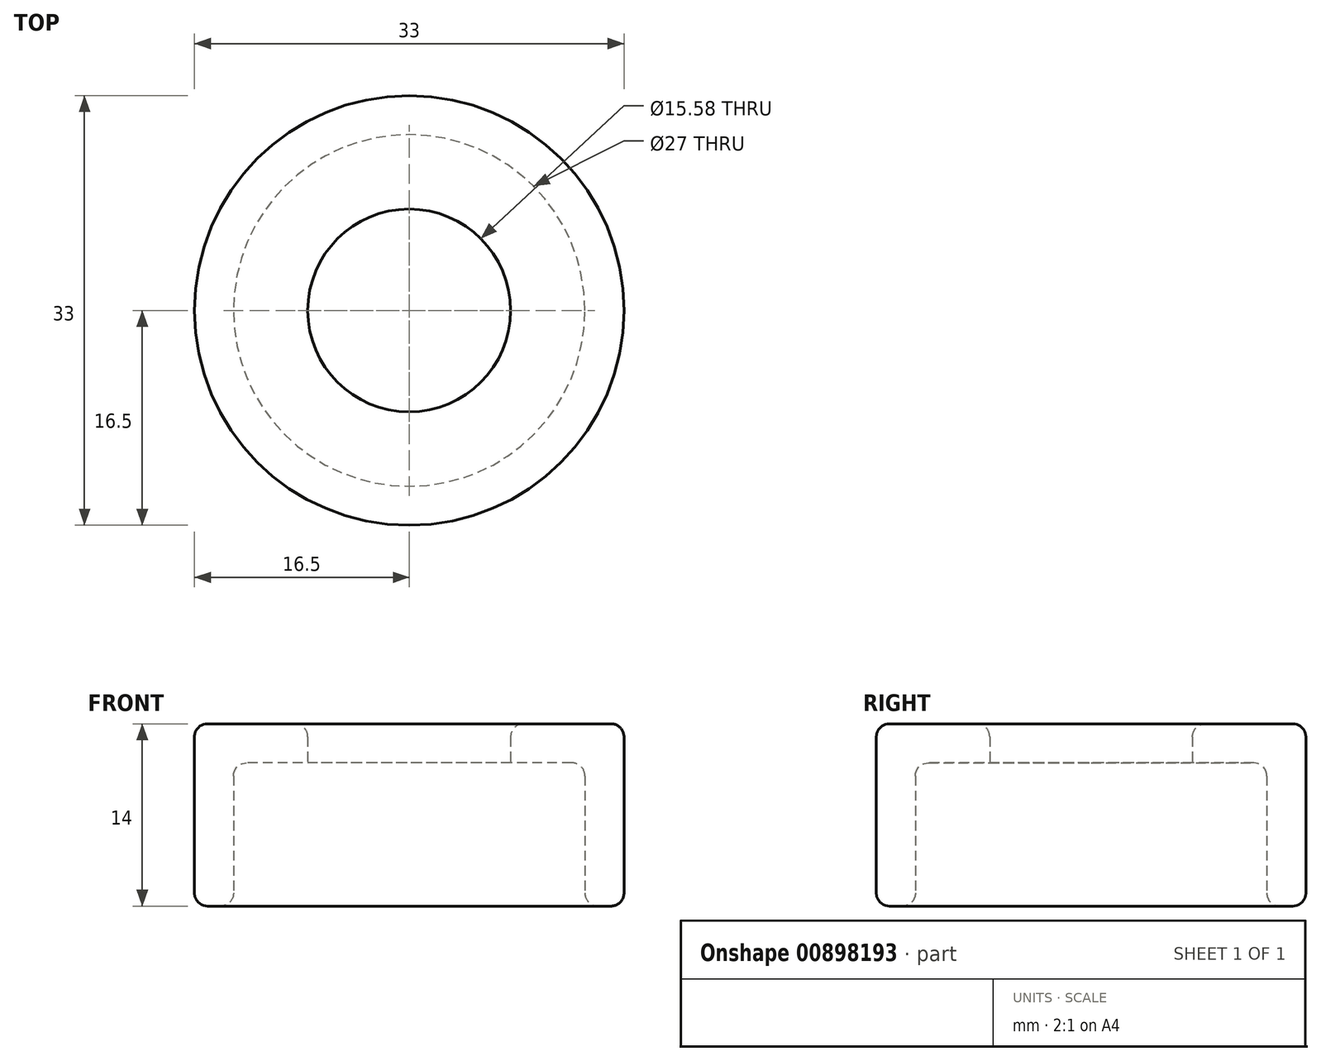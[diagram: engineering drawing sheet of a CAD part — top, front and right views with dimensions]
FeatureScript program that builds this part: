
annotation { "Feature Type Name" : "Feature", "Feature Type Description" : "" }
export const myFeature = defineFeature(function(context is Context, id is Id, definition is map)
    precondition{}
    {
        {
            var Q0;
            Q0=qCreatedBy(makeId("Front.planeOp"),FACE);
            var sketch = newSketch(context, id + "F0", { "sketchPlane" : qUnion([Q0])});
            skArc(sketch, "E0", {"start": v(4.55, -9.46) * mm, "mid": v(10.24, 2.33) * mm, "end": v(0, 10.5) * mm});
            skLineSegment(sketch, "E1.top", {"start": v(0, -17) * mm, "end": v(7, -17) * mm});
            skLineSegment(sketch, "E1.right", {"start": v(4.55, -9.46) * mm, "end": v(7, -17) * mm});
            skArc(sketch, "E2", {"start": v(10.06, -3) * mm, "mid": v(8.42, 6.27) * mm, "end": v(0, 10.5) * mm});
            skLineSegment(sketch, "E3", {"start": v(15.41, -3) * mm, "end": v(-18.62, -3) * mm, "construction": true});
            skArc(sketch, "E4", {"start": v(0, 13.5) * mm, "mid": v(10.55, 8.42) * mm, "end": v(13.16, -3) * mm});
            skLineSegment(sketch, "E5", {"start": v(-13.16, -3) * mm, "end": v(-10.06, -3) * mm});
            skLineSegment(sketch, "E6", {"start": v(10.06, -3) * mm, "end": v(13.16, -3) * mm});
            skLineSegment(sketch, "E7", {"start": v(0, -27.03) * mm, "end": v(0, 18.55) * mm, "construction": true});
            skPoint(sketch, "E8.MirrorCS.start.orphan", {"position": v(0, -17) * mm});
            skLineSegment(sketch, "E9", {"start": v(0, 13.5) * mm, "end": v(0, 10.5) * mm});
            skLineSegment(sketch, "E10", {"start": v(0, 10.5) * mm, "end": v(0, -17) * mm});
            skLineSegment(sketch, "E11", {"start": v(0, 13.5) * mm, "end": v(8, 13.5) * mm});
            skLineSegment(sketch, "E12", {"start": v(8, 13.5) * mm, "end": v(7.3, 11.36) * mm});
            skSolve(sketch);
        }
        {
            var Q0;
            {var subQ0=sQuery(id+"F0.wireOp",EDGE,"E6");var subQ4=sQuery(id+"F0.wireOp",EDGE,"E11");Q0=qUnion([makeQuery(id+"F0.imprint","IMPRINT",FACE,{"disambiguationData":[TD([[makeQuery(id+"F0.imprint","IMPRINT",EDGE,{"derivedFrom":sQuery(id+"F0.wireOp",EDGE,"E1.top")}),1.0]])]}),makeQuery(id+"F0.imprint","IMPRINT",FACE,{"disambiguationData":[TD([[makeQuery(id+"F0.imprint","IMPRINT",EDGE,{"derivedFrom":subQ4}),-1.0]])]}),makeQuery(id+"F0.imprint","IMPRINT",FACE,{"disambiguationData":[TD([[makeQuery(id+"F0.imprint","IMPRINT",EDGE,{"derivedFrom":subQ0}),1.0]])]})]);}
            var Q1;
            Q1=sQuery(id+"F0.wireOp",EDGE,"E7");
            revolve(context, id + "F1", {"surfaceOperationType" : NewSurfaceOperationType.NEW, "entities" : qUnion([Q0]), "axis" : qUnion([Q1]), "revolveType" : RevolveType.FULL});
        }
        {
            var Q0;
            Q0=qCreatedBy(makeId("Front.planeOp"),FACE);
            var sketch = newSketch(context, id + "F2", { "sketchPlane" : qUnion([Q0])});
            skLineSegment(sketch, "E13", {"start": v(-1, -3) * mm, "end": v(-1, 9) * mm});
            skLineSegment(sketch, "E14", {"start": v(1, 9) * mm, "end": v(1, -3) * mm});
            skLineSegment(sketch, "E15", {"start": v(1, -3) * mm, "end": v(-1, -3) * mm});
            skArc(sketch, "E16", {"start": v(1, 9) * mm, "mid": v(0, 10) * mm, "end": v(-1, 9) * mm});
            skLineSegment(sketch, "E17", {"start": v(-1, -3) * mm, "end": v(1, -3) * mm});
            skSolve(sketch);
        }
        {
            var Q0;
            Q0 = qSketchRegion(id + "F2", true);
            var Q1;
            Q1=makeQuery(id+"F1.opRevolve","SWEPT_FACE",FACE,{"disambiguationData":[OSD([sQuery(id+"F0.wireOp",EDGE,"E4")])]});
            extrude(context, id + "F3", {"entities" : qUnion([Q0]), "endBound" : BoundingType.UP_TO_SURFACE, "depth" : 25 * mm, "endBoundEntityFace" : qUnion([Q1]), "offsetDistance" : 25 * mm});
        }
        {
            var Q0;
            Q0=makeQuery(id+"F1.opRevolve","SWEPT_EDGE",EDGE,{"disambiguationData":[OSD([sQuery(id+"F0.wireOp",EDGE,"E0"),sQuery(id+"F0.wireOp",EDGE,"E6")])]});
            chamfer(context, id + "F4", {"entities" : qUnion([Q0]), "chamferType" : ChamferType.OFFSET_ANGLE, "width" : 2 * mm, "oppositeDirection" : false, "angle" : 72 * degree, "tangentPropagation" : true});
        }
        {
            var Q0;
            Q0=makeQuery(id+"F1.opRevolve","SWEPT_EDGE",EDGE,{"disambiguationData":[OSD([sQuery(id+"F0.wireOp",EDGE,"E4"),sQuery(id+"F0.wireOp",EDGE,"E6")])]});
            var Q1;
            {var subQ0=sQuery(id+"F0.wireOp",EDGE,"E6");Q1=makeQuery(id+"F4.opChamfer","BLEND_EDGE",EDGE,{"blendedFrom":[makeQuery(id+"F1.opRevolve","SWEPT_EDGE",EDGE,{"disambiguationData":[OSD([sQuery(id+"F0.wireOp",EDGE,"E2"),subQ0])]}),makeQuery(id+"F1.opRevolve","SWEPT_FACE",FACE,{"disambiguationData":[OSD([subQ0])]})],"blendedInto":[makeQuery(id+"F1.opRevolve","SWEPT_FACE",FACE,{"disambiguationData":[OSD([subQ0])]})]});}
            var Q2;
            Q2=makeQuery(id+"F1.opRevolve","SWEPT_EDGE",EDGE,{"disambiguationData":[OSD([sQuery(id+"F0.wireOp",EDGE,"E0"),sQuery(id+"F0.wireOp",EDGE,"E1.right")])]});
            var Q3;
            Q3=makeQuery(id+"F1.opRevolve","SWEPT_EDGE",EDGE,{"disambiguationData":[OSD([sQuery(id+"F0.wireOp",EDGE,"E1.top"),sQuery(id+"F0.wireOp",EDGE,"E1.right")])]});
            var Q4;
            Q4=makeQuery(id+"F1.opRevolve","SWEPT_EDGE",EDGE,{"disambiguationData":[OSD([sQuery(id+"F0.wireOp",EDGE,"E4"),sQuery(id+"F0.wireOp",EDGE,"E12")])]});
            var Q5;
            Q5=makeQuery(id+"F1.opRevolve","SWEPT_EDGE",EDGE,{"disambiguationData":[OSD([sQuery(id+"F0.wireOp",EDGE,"E11"),sQuery(id+"F0.wireOp",EDGE,"E12")])]});
            var Q6;
            Q6=makeQuery(id+"F4.opChamfer","BLEND_EDGE",EDGE,{"blendedFrom":[makeQuery(id+"F1.opRevolve","SWEPT_EDGE",EDGE,{"disambiguationData":[OSD([sQuery(id+"F0.wireOp",EDGE,"E0"),sQuery(id+"F0.wireOp",EDGE,"E6")])]}),makeQuery(id+"F1.opRevolve","SWEPT_FACE",FACE,{"disambiguationData":[OSD([sQuery(id+"F0.wireOp",EDGE,"E4")])]})],"blendedInto":[makeQuery(id+"F1.opRevolve","SWEPT_FACE",FACE,{"disambiguationData":[OSD([sQuery(id+"F0.wireOp",EDGE,"E4")])]})]});
            var Q7;
            {var subQ0=sQuery(id+"F0.wireOp",EDGE,"E2");Q7=makeQuery(id+"F4.opChamfer","BLEND_EDGE",EDGE,{"blendedFrom":[makeQuery(id+"F1.opRevolve","SWEPT_EDGE",EDGE,{"disambiguationData":[OSD([subQ0,sQuery(id+"F0.wireOp",EDGE,"E6")])]}),makeQuery(id+"F1.opRevolve","SWEPT_FACE",FACE,{"disambiguationData":[OSD([subQ0])]})],"blendedInto":[makeQuery(id+"F1.opRevolve","SWEPT_FACE",FACE,{"disambiguationData":[OSD([subQ0])]})]});}
            fillet(context, id + "F5", {"entities" : qUnion([Q0, Q1, Q2, Q3, Q4, Q5, Q6, Q7]), "radius" : .5 * mm, "tangentPropagation" : true, "allowEdgeOverflow" : false});
        }
        {
            var Q0;
            Q0=makeQuery(id+"F3.opExtrude","SWEPT_BODY",BODY,{"disambiguationData":[OSD([sQuery(id+"F2.wireOp",EDGE,"E13"),sQuery(id+"F2.wireOp",EDGE,"E14"),sQuery(id+"F2.wireOp",EDGE,"E16"),sQuery(id+"F2.wireOp",EDGE,"E17")])]});
            var Q1;
            Q1=sQuery(id+"F0.wireOp",EDGE,"E7");
            circularPattern(context, id + "F6", {"operationType" : NewBodyOperationType.REMOVE, "entities" : qUnion([Q0]), "axis" : qUnion([Q1]), "angle" : 360 * degree, "instanceCount" : 7, "equalSpace" : true});
        }
        {
            var Q0;
            Q0=qCreatedBy(makeId("Top.planeOp"),FACE);
            var sketch = newSketch(context, id + "F7", { "sketchPlane" : qUnion([Q0])});
            skCircle(sketch, "E18", {"center": v(0, 0) * mm, "radius": 13.5 * mm});
            skCircle(sketch, "E19", {"center": v(0, 0) * mm, "radius": 16.5 * mm});
            skCircle(sketch, "E20", {"center": v(0, 0) * mm, "radius": 7.8 * mm});
            skSolve(sketch);
        }
        {
            var Q0;
            Q0=makeQuery(id+"F7.imprint","IMPRINT",FACE,{"disambiguationData":[TD([[makeQuery(id+"F7.imprint","IMPRINT",EDGE,{"derivedFrom":sQuery(id+"F7.wireOp",EDGE,"E18")}),-1.0]])]});
            var Q1;
            Q1=makeQuery(id+"F7.imprint","IMPRINT",FACE,{"disambiguationData":[TD([[makeQuery(id+"F7.imprint","IMPRINT",EDGE,{"derivedFrom":sQuery(id+"F7.wireOp",EDGE,"E18")}),1.0]])]});
            extrude(context, id + "F8", {"entities" : qUnion([Q0, Q1]), "depth" : 14 * mm, "offsetDistance" : 25 * mm});
        }
        {
            var Q0;
            Q0=makeQuery(id+"F7.imprint","IMPRINT",FACE,{"disambiguationData":[TD([[makeQuery(id+"F7.imprint","IMPRINT",EDGE,{"derivedFrom":sQuery(id+"F7.wireOp",EDGE,"E18")}),1.0]])]});
            extrude(context, id + "F9", {"entities" : qUnion([Q0]), "operationType" : NewBodyOperationType.REMOVE, "depth" : 11 * mm, "offsetDistance" : 25 * mm});
        }
        {
            var Q0;
            Q0=makeQuery(id+"F8.opExtrude","CAP_FACE",FACE,{"disambiguationData":[OSD([sQuery(id+"F7.wireOp",EDGE,"E19"),sQuery(id+"F7.wireOp",EDGE,"E20")])],"isStart":false});
            var Q1;
            Q1=makeQuery(id+"F8.opExtrude","CAP_FACE",FACE,{"disambiguationData":[OSD([sQuery(id+"F7.wireOp",EDGE,"E19"),sQuery(id+"F7.wireOp",EDGE,"E20")])],"isStart":true});
            var Q2;
            Q2=makeQuery(id+"F9.boolean.opBoolean","COPY",EDGE,{"derivedFrom":makeQuery(id+"F9.opExtrude","CAP_EDGE",EDGE,{"disambiguationData":[OSD([sQuery(id+"F7.wireOp",EDGE,"E20")])],"isStart":false})});
            var Q3;
            Q3=makeQuery(id+"F9.boolean.opBoolean","COPY",EDGE,{"derivedFrom":makeQuery(id+"F9.opExtrude","CAP_EDGE",EDGE,{"disambiguationData":[OSD([sQuery(id+"F7.wireOp",EDGE,"E18")])],"isStart":false})});
            fillet(context, id + "F10", {"entities" : qUnion([Q0, Q1, Q2, Q3]), "radius" : 1 * mm, "tangentPropagation" : true, "allowEdgeOverflow" : false});
        }
    });
